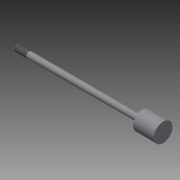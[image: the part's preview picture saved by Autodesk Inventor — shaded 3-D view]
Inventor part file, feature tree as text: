
AUTODESK INVENTOR PART (.ipt)
format: ipt  version: 2014 SP2 (Build 180246200, 246)  size: 141,312 bytes
history: native  units: in
note: dims shown in document units (in); Inventor stores cm internally (conversion verified against a paired STEP export)
features: other x84, revolve x3, sketch x3, thread x1
ambient origin geometry x8: Origin, YZ Plane, XZ Plane, XY Plane, X Axis, Y Axis, Z Axis, Center Point
bodies: Solid1 (feature_tree)
feature tree (91):
  revolve  "Revolution1"  Angle=360.0deg
  revolve  "Revolution2"  Angle=360.0deg
  thread  "Thread1"  [1 undecoded]
  revolve  "Revolution3"  [1 undecoded]
  other  "dia1_XY"
  other  "dia1_YZ"
  other  "dia1_ZX"
  other  "dia1_X"
  other  "dia1_Y"
  other  "dia1_Z"
  other  "dia1_Center"
  other  "dia12_XY"
  other  "dia12_YZ"
  other  "dia12_ZX"
  other  "dia12_X"
  other  "dia12_Y"
  other  "dia12_Z"
  other  "dia12_Center"
  other  "dia2_XY"
  other  "dia2_YZ"
  other  "dia2_ZX"
  other  "dia2_X"
  other  "dia2_Y"
  other  "dia2_Z"
  other  "dia2_Center"
  other  "dia22_XY"
  other  "dia22_YZ"
  other  "dia22_ZX"
  other  "dia22_X"
  other  "dia22_Y"
  other  "dia22_Z"
  other  "dia22_Center"
  other  "hh1_XY"
  other  "hh1_YZ"
  other  "hh1_ZX"
  other  "hh1_X"
  other  "hh1_Y"
  other  "hh1_Z"
  other  "hh1_Center"
  other  "hh2_XY"
  other  "hh2_YZ"
  other  "hh2_ZX"
  other  "hh2_X"
  other  "hh2_Y"
  other  "hh2_Z"
  other  "hh2_Center"
  other  "rl1_XY"
  other  "rl1_YZ"
  other  "rl1_ZX"
  other  "rl1_X"
  other  "rl1_Y"
  other  "rl1_Z"
  other  "rl1_Center"
  other  "rl2_XY"
  other  "rl2_YZ"
  other  "rl2_ZX"
  other  "rl2_X"
  other  "rl2_Y"
  other  "rl2_Z"
  other  "rl2_Center"
  other  "rod_cp_XY"
  other  "rod_cp_YZ"
  other  "rod_cp_ZX"
  other  "rod_cp_X"
  other  "rod_cp_Y"
  other  "rod_cp_Z"
  other  "rod_cp_Center"
  other  "thd1_XY"
  other  "thd1_YZ"
  other  "thd1_ZX"
  other  "thd1_X"
  other  "thd1_Y"
  other  "thd1_Z"
  other  "thd1_Center"
  other  "thd2_XY"
  other  "thd2_YZ"
  other  "thd2_ZX"
  other  "thd2_X"
  other  "thd2_Y"
  other  "thd2_Z"
  other  "thd2_Center"
  other  "to_rod_clevis_XY"
  other  "to_rod_clevis_YZ"
  other  "to_rod_clevis_ZX"
  other  "to_rod_clevis_X"
  other  "to_rod_clevis_Y"
  other  "to_rod_clevis_Z"
  other  "to_rod_clevis_Center"
  sketch  "Sketch_1"  dims[d0=360.0deg d1=360.0deg]
  sketch  "Sketch_3"  dims[d2=0.4787in d3=0.0in d4=360.0deg]
  sketch  "Sketch_30"  dims[d5=0.0in d6=0.0in d7=0.0in d8=0.0in d9=0.0in]
note: 2 required parameter values undecoded (feature->parameter linkage not recoverable at this tier; creation-order binding heuristic only, values carry confidence <= 0.55)
